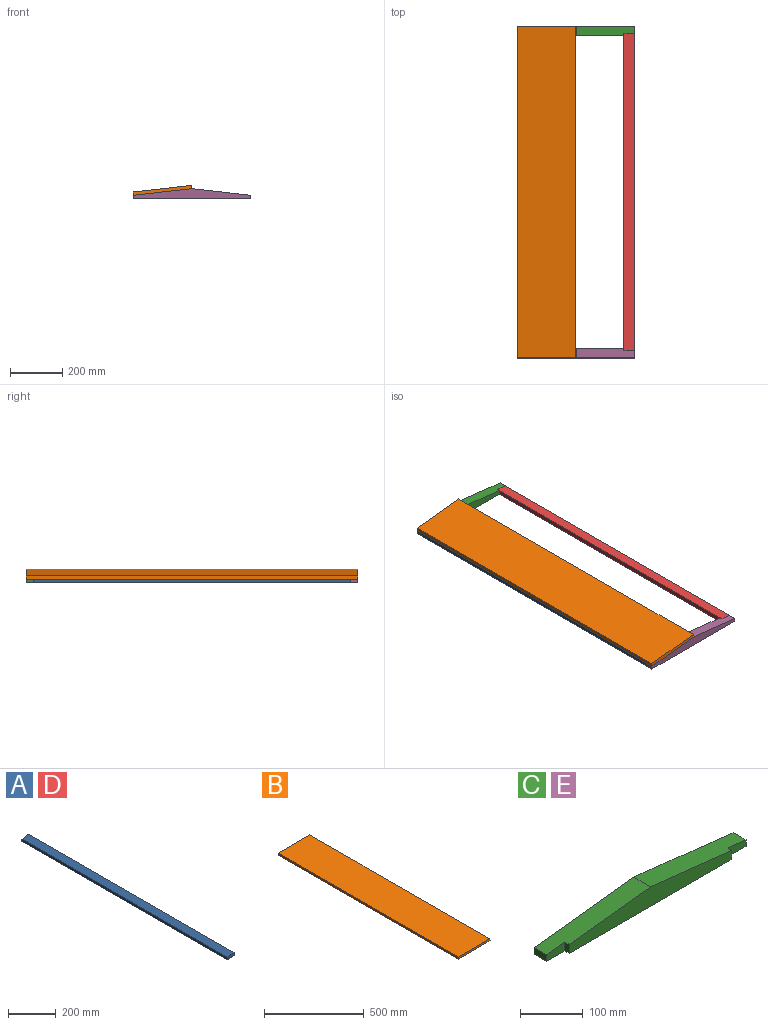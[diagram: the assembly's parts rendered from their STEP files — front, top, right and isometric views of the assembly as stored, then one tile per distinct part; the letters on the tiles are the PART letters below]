
ASSEMBLY  parts=5 mates=4
PART A: 6 faces, bbox 41.3x1219.2x17.4 mm
  f0: plane 1219.2x41.28mm, normal (-0.11,0,0.99), area 50641mm2, adj f1,f3,f4,f5
  f1: plane 1219.2x12.7mm, normal (-1,0,0), area 15483.8mm2, adj f0,f2,f4,f5
  f2: plane 1219.2x41.28mm, normal (0,0,-1), area 50322.5mm2, adj f1,f3,f4,f5
  f3: plane 1219.2x17.35mm, normal (1,0,0), area 21155.1mm2, adj f0,f2,f4,f5
  f4: plane 41.28x17.35mm, normal (0,-1,0), area 620.2mm2, adj f0,f1,f2,f3
  f5: plane 41.28x17.35mm, normal (0,1,0), area 620.2mm2, adj f0,f1,f2,f3
PART B: 6 faces, bbox 226.8x1276.4x12.7 mm
  f0: plane 1276.35x225.42mm, normal (0,0,1), area 287718.5mm2, adj f1,f3,f4,f5
  f1: plane 1276.35x12.7mm, normal (-1,0,0), area 16209.6mm2, adj f0,f2,f4,f5
  f2: plane 1276.35x226.85mm, normal (0,0,-1), area 289536.7mm2, adj f1,f3,f4,f5
  f3: plane 1276.35x12.7mm, normal (0.99,0,0.11), area 16311.3mm2, adj f0,f2,f4,f5
  f4: plane 226.85x12.7mm, normal (0,-1,0), area 2871.9mm2, adj f0,f1,f2,f3
  f5: plane 226.85x12.7mm, normal (0,1,0), area 2871.9mm2, adj f0,f1,f2,f3
PART C: 11 faces, bbox 450.9x38.1x38.1 mm
  f0: plane 28.58x12.7mm, normal (1,0,0), area 362.9mm2, adj f1,f2,f6,f9
  f1: plane 450.85x38.1mm, normal (0,0,-1), area 16391.1mm2, adj f0,f3,f4,f6,f7,f8,f9,f10
  f2: plane 225.43x38.1mm, normal (0.11,0,0.99), area 8247.4mm2, adj f0,f3,f5,f6,f9,f10
  f3: plane 368.3x38.1mm, normal (0,-1,0), area 10211.2mm2, adj f1,f2,f5,f8,f10
  f4: plane 28.58x12.7mm, normal (-1,0,0), area 362.9mm2, adj f1,f5,f6,f7
  f5: plane 225.43x38.1mm, normal (-0.11,0,0.99), area 8247.4mm2, adj f2,f3,f4,f6,f7,f8
  f6: plane 450.85x38.1mm, normal (0,1,0), area 11451.6mm2, adj f0,f1,f2,f4,f5
  f7: plane 41.28x17.35mm, normal (0,-1,0), area 620.2mm2, adj f1,f4,f5,f8
  f8: plane 17.35x9.53mm, normal (-1,0,0), area 165.3mm2, adj f1,f3,f5,f7
  f9: plane 41.28x17.35mm, normal (0,-1,0), area 620.2mm2, adj f0,f1,f2,f10
  f10: plane 17.35x9.53mm, normal (1,0,0), area 165.3mm2, adj f1,f2,f3,f9
PART D: same geometry as A
PART E: same geometry as C
PLACE A t=(-72,-577.53,-46.7)mm
PLACE B rot(axis=(0.06,0,-1),180deg) t=(44.66,-577.53,-18.67)mm
PLACE C t=(129.18,60.65,-38.67)mm fixed
PLACE D rot(axis=(0,0,-1),180deg) t=(330.36,-577.53,-46.7)mm
PLACE E rot(axis=(0,0,-1),180deg) t=(129.18,-1215.7,-38.67)mm
MATE fastened A.f0 <-> B.f2  axis (-0.11,0,0.99) through (-96.25,-577.53,-34)mm
MATE fastened D.f5 <-> E.f7  axis (0,-1,0) through (354.6,-1187.13,-40.35)mm
MATE fastened C.f7 <-> A.f5  axis (0,-1,0) through (-75.61,32.07,-31.68)mm
MATE fastened A.f4 <-> E.f9  axis (0,-1,0) through (-96.25,-1187.13,-40.35)mm
